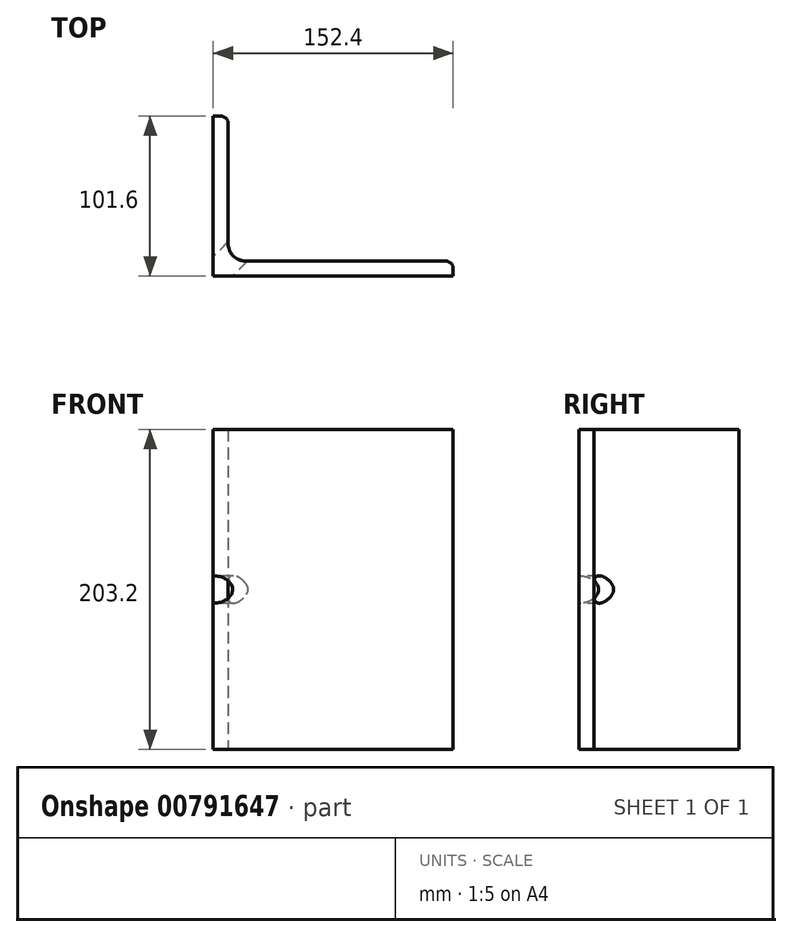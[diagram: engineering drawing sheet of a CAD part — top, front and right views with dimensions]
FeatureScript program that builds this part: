
annotation { "Feature Type Name" : "Feature", "Feature Type Description" : "" }
export const myFeature = defineFeature(function(context is Context, id is Id, definition is map)
    precondition{}
    {
        {
            var Q0;
            Q0=qCreatedBy(makeId("Top.planeOp"),FACE);
            var sketch = newSketch(context, id + "F0", { "sketchPlane" : qUnion([Q0])});
            skLineSegment(sketch, "E0", {"start": v(0, 0) * mm, "end": v(0, 101.6) * mm});
            skLineSegment(sketch, "E1", {"start": v(0, 101.6) * mm, "end": v(4.76, 101.6) * mm});
            skLineSegment(sketch, "E2", {"start": v(9.53, 96.84) * mm, "end": v(9.53, 20.64) * mm});
            skLineSegment(sketch, "E3", {"start": v(20.64, 9.52) * mm, "end": v(147.64, 9.53) * mm});
            skLineSegment(sketch, "E4", {"start": v(152.4, 4.76) * mm, "end": v(152.4, 0) * mm});
            skLineSegment(sketch, "E5", {"start": v(152.4, 0) * mm, "end": v(0, 0) * mm});
            skPoint(sketch, "E6.visualSharp", {"position": v(9.53, 101.6) * mm});
            skArc(sketch, "E6.filletArc", {"start": v(9.53, 96.84) * mm, "mid": v(8.13, 100.2) * mm, "end": v(4.76, 101.6) * mm});
            skPoint(sketch, "E7.visualSharp", {"position": v(152.4, 9.53) * mm});
            skArc(sketch, "E7.filletArc", {"start": v(152.4, 4.76) * mm, "mid": v(151, 8.13) * mm, "end": v(147.64, 9.53) * mm});
            skPoint(sketch, "E8.visualSharp", {"position": v(9.53, 9.52) * mm});
            skArc(sketch, "E8.filletArc", {"start": v(9.53, 20.64) * mm, "mid": v(12.78, 12.78) * mm, "end": v(20.64, 9.52) * mm});
            skSolve(sketch);
        }
        {
            var Q0;
            Q0=makeQuery(id+"F0.imprint","IMPRINT",FACE,{"disambiguationData":[TD([[makeQuery(id+"F0.imprint","IMPRINT",EDGE,{"derivedFrom":sQuery(id+"F0.wireOp",EDGE,"E0")}),-1.0]])]});
            extrude(context, id + "F1", {"entities" : qUnion([Q0]), "endBound" : BoundingType.SYMMETRIC, "depth" : 203.2 * mm, "offsetDistance" : 25.4 * mm});
        }
        {
            var Q0;
            Q0=makeQuery(id+"F1.opExtrude","SWEPT_EDGE",EDGE,{"disambiguationData":[OSD([sQuery(id+"F0.wireOp",EDGE,"E0"),sQuery(id+"F0.wireOp",EDGE,"E5")])]});
            cPlane(context, id + "F2", {"entities" : qUnion([Q0]), "cplaneType" : CPlaneType.LINE_ANGLE, "offset" : 0 * mm, "angle" : 135 * degree, "width" : 152.4 * mm, "height" : 152.4 * mm});
        }
        {
            var Q0;
            Q0=qCreatedBy(id+"F2.planeOp",FACE);
            var sketch = newSketch(context, id + "F3", { "sketchPlane" : qUnion([Q0])});
            skCircle(sketch, "E9", {"center": v(0, 0) * mm, "radius": 8.73 * mm});
            skSolve(sketch);
        }
        {
            var Q0;
            Q0=makeQuery(id+"F3.imprint","IMPRINT",FACE,{"disambiguationData":[TD([[makeQuery(id+"F3.imprint","IMPRINT",EDGE,{"derivedFrom":sQuery(id+"F3.wireOp",EDGE,"E9")}),1.0]])]});
            extrude(context, id + "F4", {"entities" : qUnion([Q0]), "operationType" : NewBodyOperationType.REMOVE, "depth" : 25.4 * mm, "offsetDistance" : 25.4 * mm});
        }
    });
